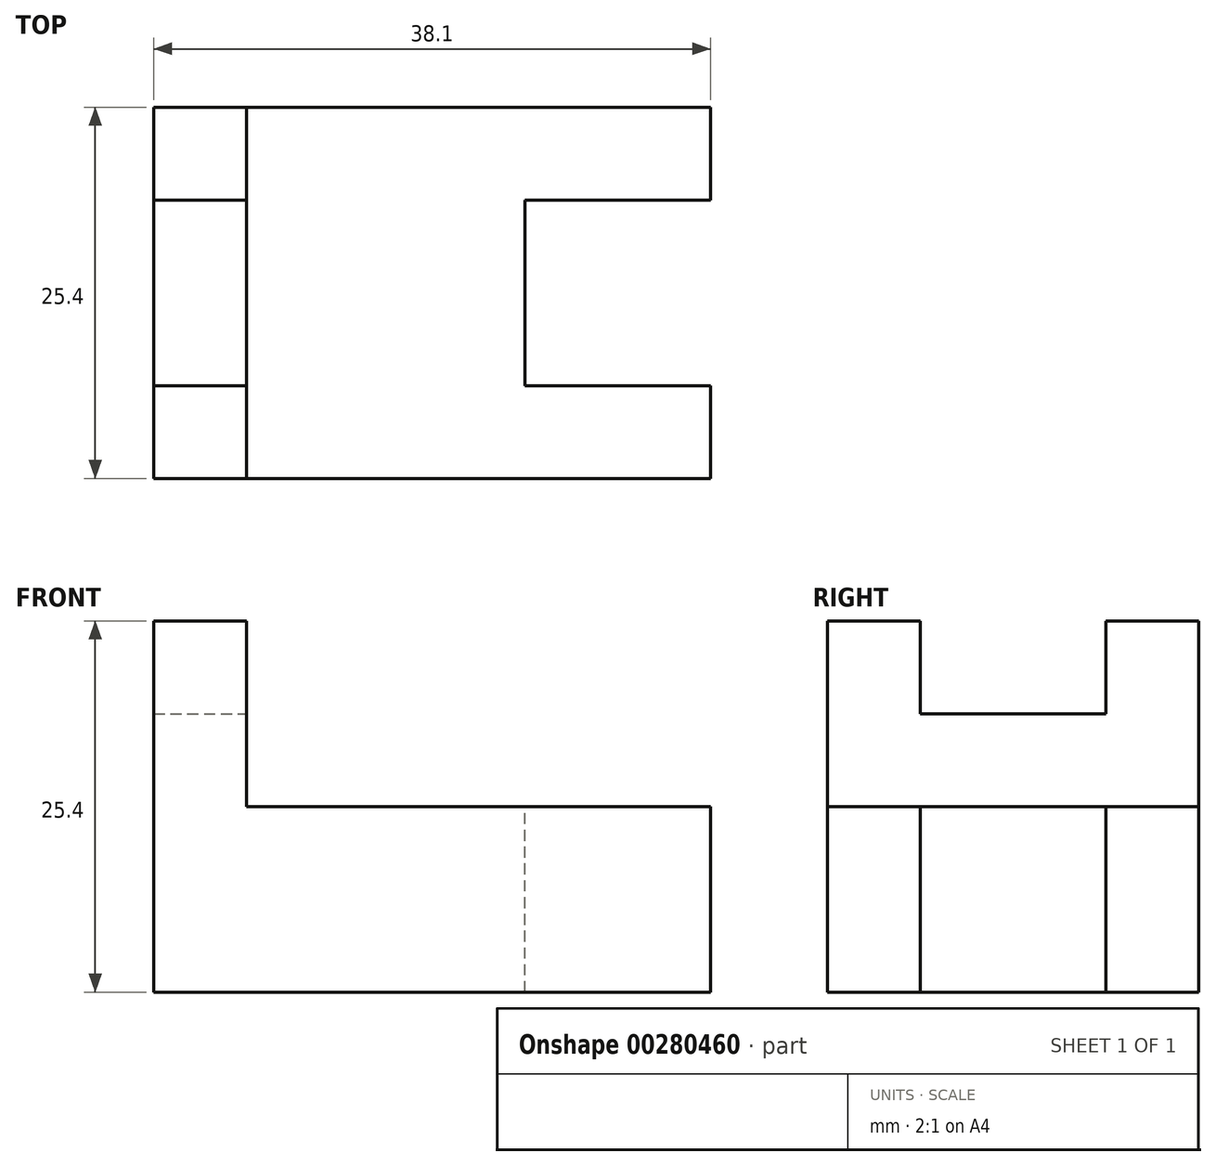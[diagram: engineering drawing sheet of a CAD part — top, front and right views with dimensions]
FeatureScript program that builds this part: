
annotation { "Feature Type Name" : "Feature", "Feature Type Description" : "" }
export const myFeature = defineFeature(function(context is Context, id is Id, definition is map)
    precondition{}
    {
        {
            var Q0;
            Q0=qCreatedBy(makeId("Front.planeOp"),FACE);
            var sketch = newSketch(context, id + "F0", { "sketchPlane" : qUnion([Q0])});
            skLineSegment(sketch, "E0", {"start": v(0, 0) * mm, "end": v(0, 25.4) * mm});
            skLineSegment(sketch, "E1", {"start": v(0, 25.4) * mm, "end": v(6.35, 25.4) * mm});
            skLineSegment(sketch, "E2", {"start": v(6.35, 25.4) * mm, "end": v(6.35, 12.7) * mm});
            skLineSegment(sketch, "E3", {"start": v(6.35, 12.7) * mm, "end": v(38.1, 12.7) * mm});
            skLineSegment(sketch, "E4", {"start": v(38.1, 12.7) * mm, "end": v(38.1, 0) * mm});
            skLineSegment(sketch, "E5", {"start": v(38.1, 0) * mm, "end": v(0, 0) * mm});
            skSolve(sketch);
        }
        {
            var Q0;
            Q0=makeQuery(id+"F0.imprint","IMPRINT",FACE,{"disambiguationData":[TD([[makeQuery(id+"F0.imprint","IMPRINT",EDGE,{"derivedFrom":sQuery(id+"F0.wireOp",EDGE,"E0")}),-1.0]])]});
            extrude(context, id + "F1", {"entities" : qUnion([Q0]), "endBound" : BoundingType.SYMMETRIC, "depth" : 25.4 * mm});
        }
        {
            var Q0;
            Q0=makeQuery(id+"F1.opExtrude","SWEPT_FACE",FACE,{"disambiguationData":[OSD([sQuery(id+"F0.wireOp",EDGE,"E3")])]});
            var sketch = newSketch(context, id + "F2", { "sketchPlane" : qUnion([Q0])});
            skLineSegment(sketch, "E6.bottom", {"start": v(38.1, 6.35) * mm, "end": v(25.4, 6.35) * mm});
            skLineSegment(sketch, "E6.top", {"start": v(38.1, -6.35) * mm, "end": v(25.4, -6.35) * mm});
            skLineSegment(sketch, "E6.left", {"start": v(38.1, 6.35) * mm, "end": v(38.1, -6.35) * mm});
            skLineSegment(sketch, "E6.right", {"start": v(25.4, 6.35) * mm, "end": v(25.4, -6.35) * mm});
            skSolve(sketch);
        }
        {
            var Q0;
            Q0=makeQuery(id+"F2.imprint","IMPRINT",FACE,{"disambiguationData":[TD([[makeQuery(id+"F2.imprint","IMPRINT",EDGE,{"derivedFrom":sQuery(id+"F2.wireOp",EDGE,"E6.bottom")}),1.0]])]});
            extrude(context, id + "F3", {"entities" : qUnion([Q0]), "operationType" : NewBodyOperationType.REMOVE, "endBound" : BoundingType.THROUGH_ALL, "oppositeDirection" : true, "depth" : 25.4 * mm});
        }
        {
            var Q0;
            Q0=makeQuery(id+"F1.opExtrude","SWEPT_FACE",FACE,{"disambiguationData":[OSD([sQuery(id+"F0.wireOp",EDGE,"E1")])]});
            var sketch = newSketch(context, id + "F4", { "sketchPlane" : qUnion([Q0])});
            skLineSegment(sketch, "E7.bottom", {"start": v(0, 6.35) * mm, "end": v(6.35, 6.35) * mm});
            skLineSegment(sketch, "E7.top", {"start": v(0, -6.35) * mm, "end": v(6.35, -6.35) * mm});
            skLineSegment(sketch, "E7.left", {"start": v(0, 6.35) * mm, "end": v(0, -6.35) * mm});
            skLineSegment(sketch, "E7.right", {"start": v(6.35, 6.35) * mm, "end": v(6.35, -6.35) * mm});
            skSolve(sketch);
        }
        {
            var Q0;
            Q0=makeQuery(id+"F4.imprint","IMPRINT",FACE,{"disambiguationData":[TD([[makeQuery(id+"F4.imprint","IMPRINT",EDGE,{"derivedFrom":sQuery(id+"F4.wireOp",EDGE,"E7.bottom")}),-1.0]])]});
            extrude(context, id + "F5", {"entities" : qUnion([Q0]), "operationType" : NewBodyOperationType.REMOVE, "oppositeDirection" : true, "depth" : 6.35 * mm});
        }
    });
